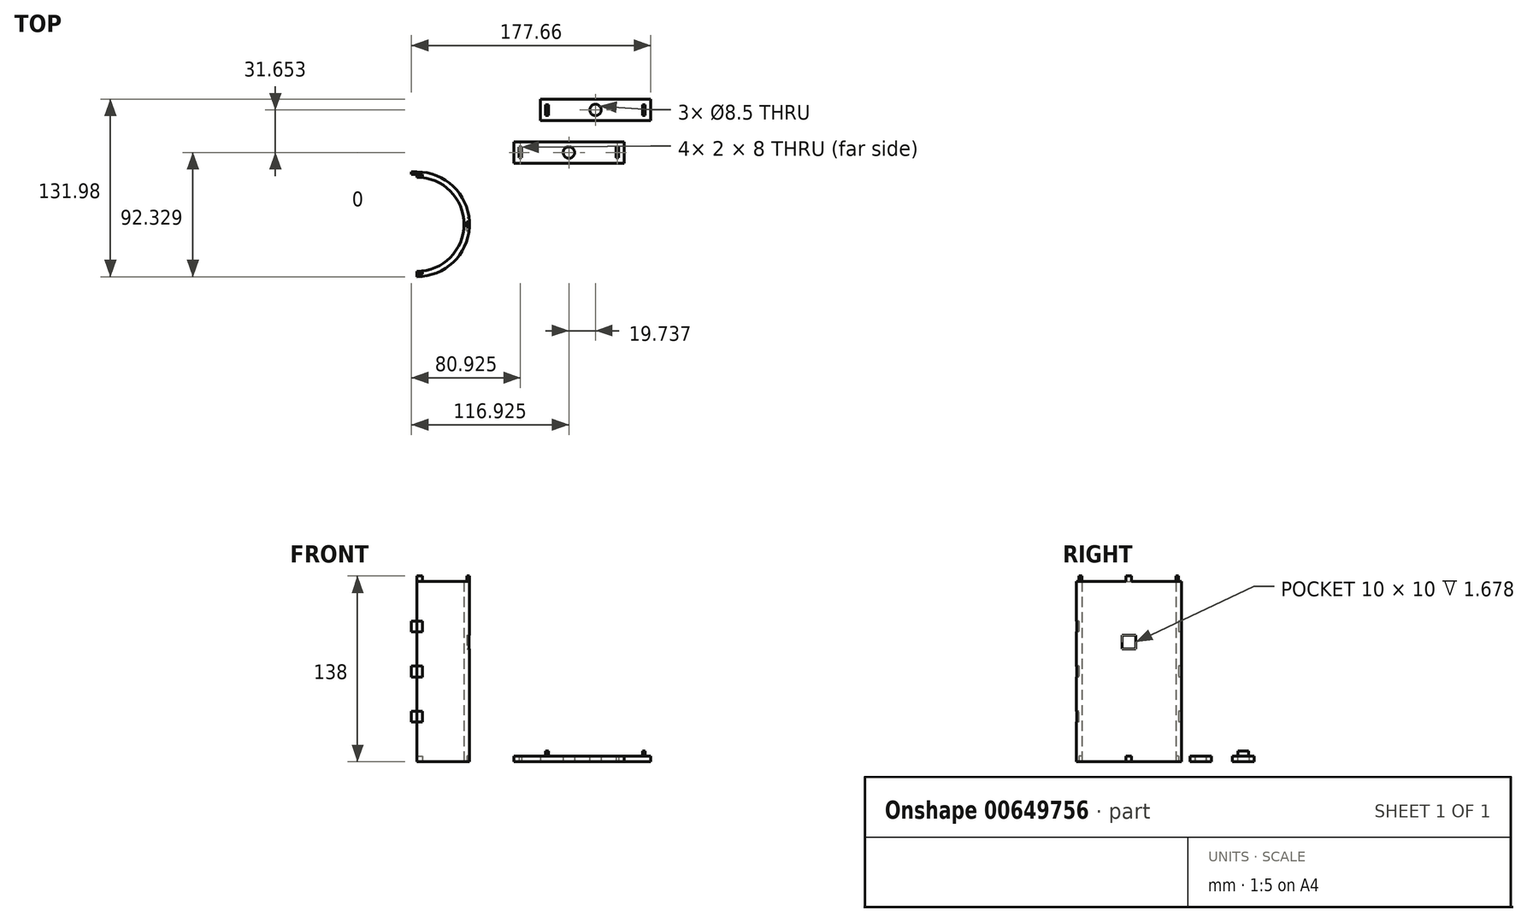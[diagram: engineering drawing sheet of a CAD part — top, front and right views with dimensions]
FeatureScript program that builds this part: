
annotation { "Feature Type Name" : "Feature", "Feature Type Description" : "" }
export const myFeature = defineFeature(function(context is Context, id is Id, definition is map)
    precondition{}
    {
        {
            var Q0;
            Q0=qCreatedBy(makeId("Top.planeOp"),FACE);
            var sketch = newSketch(context, id + "F0", { "sketchPlane" : qUnion([Q0])});
            skCircle(sketch, "E0", {"center": v(0, 0) * mm, "radius": 35 * mm});
            skCircle(sketch, "E1", {"center": v(0, 0) * mm, "radius": 39 * mm});
            skLineSegment(sketch, "E2", {"start": v(0, 39) * mm, "end": v(0, -39) * mm});
            skPoint(sketch, "E3", {"position": v(0, 35) * mm});
            skPoint(sketch, "E4", {"position": v(0, -35) * mm});
            skLineSegment(sketch, "E5.bottom", {"start": v(0, 35) * mm, "end": v(4, 35) * mm});
            skLineSegment(sketch, "E5.top", {"start": v(0, 37) * mm, "end": v(4, 37) * mm});
            skLineSegment(sketch, "E5.left", {"start": v(0, 35) * mm, "end": v(0, 37) * mm});
            skLineSegment(sketch, "E5.right", {"start": v(4, 35) * mm, "end": v(4, 37) * mm});
            skLineSegment(sketch, "E6.bottom", {"start": v(0, -35) * mm, "end": v(4, -35) * mm});
            skLineSegment(sketch, "E6.top", {"start": v(0, -37) * mm, "end": v(4, -37) * mm});
            skLineSegment(sketch, "E6.left", {"start": v(0, -35) * mm, "end": v(0, -37) * mm});
            skLineSegment(sketch, "E6.right", {"start": v(4, -35) * mm, "end": v(4, -37) * mm});
            skLineSegment(sketch, "E7", {"start": v(0, 0) * mm, "end": v(39, 0) * mm, "construction": true});
            skLineSegment(sketch, "E8.bottom", {"start": v(39, 2) * mm, "end": v(37, 2) * mm});
            skLineSegment(sketch, "E8.top", {"start": v(39, -2) * mm, "end": v(37, -2) * mm});
            skLineSegment(sketch, "E8.left", {"start": v(39, 2) * mm, "end": v(39, -2) * mm});
            skLineSegment(sketch, "E8.right", {"start": v(37, 2) * mm, "end": v(37, -2) * mm});
            skPoint(sketch, "E9", {"position": v(39, 0) * mm});
            skSolve(sketch);
        }
        {
            var Q0;
            {var subQ2=sQuery(id+"F0.wireOp",EDGE,"E5.bottom");Q0=makeQuery(id+"F0.imprint","IMPRINT",FACE,{"disambiguationData":[TD([[makeQuery(id+"F0.imprint","IMPRINT",EDGE,{"derivedFrom":subQ2}),-1.0]])]});}
            var Q1;
            Q1=makeQuery(id+"F0.imprint","IMPRINT",FACE,{"disambiguationData":[TD([[makeQuery(id+"F0.imprint","IMPRINT",EDGE,{"derivedFrom":sQuery(id+"F0.wireOp",EDGE,"E6.bottom")}),-1.0]])]});
            var Q2;
            Q2=makeQuery(id+"F0.imprint","IMPRINT",FACE,{"disambiguationData":[TD([[makeQuery(id+"F0.imprint","IMPRINT",EDGE,{"derivedFrom":sQuery(id+"F0.wireOp",EDGE,"E5.bottom")}),1.0]])]});
            var Q3;
            {var subQ0=sQuery(id+"F0.wireOp",EDGE,"E8.right");Q3=makeQuery(id+"F0.imprint","IMPRINT",FACE,{"disambiguationData":[TD([[makeQuery(id+"F0.imprint","IMPRINT",EDGE,{"derivedFrom":subQ0}),1.0]])]});}
            extrude(context, id + "F1", {"entities" : qUnion([Q0, Q1, Q2, Q3]), "depth" : 134 * mm, "offsetDistance" : 25 * mm});
        }
        {
            var Q0;
            Q0=makeQuery(id+"F0.imprint","IMPRINT",FACE,{"disambiguationData":[TD([[makeQuery(id+"F0.imprint","IMPRINT",EDGE,{"derivedFrom":sQuery(id+"F0.wireOp",EDGE,"E6.bottom")}),-1.0]])]});
            var Q1;
            {var subQ0=sQuery(id+"F0.wireOp",EDGE,"E8.right");Q1=makeQuery(id+"F0.imprint","IMPRINT",FACE,{"disambiguationData":[TD([[makeQuery(id+"F0.imprint","IMPRINT",EDGE,{"derivedFrom":subQ0}),1.0]])]});}
            var Q2;
            Q2=makeQuery(id+"F0.imprint","IMPRINT",FACE,{"disambiguationData":[TD([[makeQuery(id+"F0.imprint","IMPRINT",EDGE,{"derivedFrom":sQuery(id+"F0.wireOp",EDGE,"E5.bottom")}),1.0]])]});
            extrude(context, id + "F2", {"entities" : qUnion([Q0, Q1, Q2]), "operationType" : NewBodyOperationType.ADD, "depth" : 138 * mm, "offsetDistance" : 25 * mm});
        }
        {
            var Q0;
            Q0=makeQuery(id+"F0.imprint","IMPRINT",FACE,{"disambiguationData":[TD([[makeQuery(id+"F0.imprint","IMPRINT",EDGE,{"derivedFrom":sQuery(id+"F0.wireOp",EDGE,"E6.bottom")}),-1.0]])]});
            var Q1;
            {var subQ0=sQuery(id+"F0.wireOp",EDGE,"E8.right");Q1=makeQuery(id+"F0.imprint","IMPRINT",FACE,{"disambiguationData":[TD([[makeQuery(id+"F0.imprint","IMPRINT",EDGE,{"derivedFrom":subQ0}),1.0]])]});}
            var Q2;
            Q2=makeQuery(id+"F0.imprint","IMPRINT",FACE,{"disambiguationData":[TD([[makeQuery(id+"F0.imprint","IMPRINT",EDGE,{"derivedFrom":sQuery(id+"F0.wireOp",EDGE,"E5.bottom")}),1.0]])]});
            extrude(context, id + "F3", {"entities" : qUnion([Q0, Q1, Q2]), "operationType" : NewBodyOperationType.REMOVE, "oppositeDirection" : true, "depth" : 4 * mm, "offsetDistance" : 25 * mm});
        }
        {
            var Q0;
            Q0=makeQuery(id+"F0.imprint","IMPRINT",FACE,{"disambiguationData":[TD([[makeQuery(id+"F0.imprint","IMPRINT",EDGE,{"derivedFrom":sQuery(id+"F0.wireOp",EDGE,"E6.bottom")}),-1.0]])]});
            var Q1;
            {var subQ0=sQuery(id+"F0.wireOp",EDGE,"E8.right");Q1=makeQuery(id+"F0.imprint","IMPRINT",FACE,{"disambiguationData":[TD([[makeQuery(id+"F0.imprint","IMPRINT",EDGE,{"derivedFrom":subQ0}),1.0]])]});}
            var Q2;
            Q2=makeQuery(id+"F0.imprint","IMPRINT",FACE,{"disambiguationData":[TD([[makeQuery(id+"F0.imprint","IMPRINT",EDGE,{"derivedFrom":sQuery(id+"F0.wireOp",EDGE,"E5.bottom")}),1.0]])]});
            extrude(context, id + "F4", {"entities" : qUnion([Q0, Q1, Q2]), "operationType" : NewBodyOperationType.REMOVE, "oppositeDirection" : true, "depth" : -4 * mm, "offsetDistance" : 25 * mm});
        }
        {
            var Q0;
            {var subQ0=sQuery(id+"F0.wireOp",EDGE,"E5.left");Q0=makeQuery(id+"F2.boolean.opBoolean","MERGE",FACE,{"derivedFrom":[makeQuery(id+"F1.opExtrude","SWEPT_FACE",FACE,{"disambiguationData":[OSD([sQuery(id+"F0.wireOp",EDGE,"E2"),subQ0])]}),makeQuery(id+"F2.opExtrude","SWEPT_FACE",FACE,{"disambiguationData":[OSD([subQ0])]})]});}
            var sketch = newSketch(context, id + "F5", { "sketchPlane" : qUnion([Q0])});
            skLineSegment(sketch, "E10", {"start": v(-39, 134) * mm, "end": v(-39, 0) * mm, "construction": true});
            skPoint(sketch, "E11", {"position": v(-39, 67) * mm});
            skLineSegment(sketch, "E12", {"start": v(-39, 0) * mm, "end": v(39, 0) * mm, "construction": true});
            skLineSegment(sketch, "E13", {"start": v(39, 134) * mm, "end": v(39, 0) * mm, "construction": true});
            skPoint(sketch, "E14", {"position": v(39, 67) * mm});
            skLineSegment(sketch, "E15.bottom", {"start": v(-39, 71) * mm, "end": v(-37, 71) * mm});
            skLineSegment(sketch, "E15.top", {"start": v(-39, 63) * mm, "end": v(-37, 63) * mm});
            skLineSegment(sketch, "E15.left", {"start": v(-39, 71) * mm, "end": v(-39, 63) * mm});
            skLineSegment(sketch, "E15.right", {"start": v(-37, 71) * mm, "end": v(-37, 63) * mm});
            skLineSegment(sketch, "E16.bottom", {"start": v(37, 71) * mm, "end": v(39, 71) * mm});
            skLineSegment(sketch, "E16.top", {"start": v(37, 63) * mm, "end": v(39, 63) * mm});
            skLineSegment(sketch, "E16.left", {"start": v(37, 71) * mm, "end": v(37, 63) * mm});
            skLineSegment(sketch, "E16.right", {"start": v(39, 71) * mm, "end": v(39, 63) * mm});
            skPoint(sketch, "E17", {"position": v(-39, 100.5) * mm});
            skPoint(sketch, "E18", {"position": v(39, 100.5) * mm});
            skPoint(sketch, "E19", {"position": v(39, 33.5) * mm});
            skPoint(sketch, "E20", {"position": v(-39, 33.5) * mm});
            skLineSegment(sketch, "E21.bottom", {"start": v(-39, 104.5) * mm, "end": v(-37, 104.5) * mm});
            skLineSegment(sketch, "E21.top", {"start": v(-39, 96.5) * mm, "end": v(-37, 96.5) * mm});
            skLineSegment(sketch, "E21.left", {"start": v(-39, 104.5) * mm, "end": v(-39, 96.5) * mm});
            skLineSegment(sketch, "E21.right", {"start": v(-37, 104.5) * mm, "end": v(-37, 96.5) * mm});
            skLineSegment(sketch, "E22.bottom", {"start": v(-39, 37.5) * mm, "end": v(-37, 37.5) * mm});
            skLineSegment(sketch, "E22.top", {"start": v(-39, 29.5) * mm, "end": v(-37, 29.5) * mm});
            skLineSegment(sketch, "E22.left", {"start": v(-39, 37.5) * mm, "end": v(-39, 29.5) * mm});
            skLineSegment(sketch, "E22.right", {"start": v(-37, 37.5) * mm, "end": v(-37, 29.5) * mm});
            skLineSegment(sketch, "E23.bottom", {"start": v(37, 104.5) * mm, "end": v(39, 104.5) * mm});
            skLineSegment(sketch, "E23.top", {"start": v(37, 96.5) * mm, "end": v(39, 96.5) * mm});
            skLineSegment(sketch, "E23.left", {"start": v(37, 104.5) * mm, "end": v(37, 96.5) * mm});
            skLineSegment(sketch, "E23.right", {"start": v(39, 104.5) * mm, "end": v(39, 96.5) * mm});
            skLineSegment(sketch, "E24.bottom", {"start": v(37, 29.5) * mm, "end": v(39, 29.5) * mm});
            skLineSegment(sketch, "E24.top", {"start": v(37, 37.5) * mm, "end": v(39, 37.5) * mm});
            skLineSegment(sketch, "E24.left", {"start": v(37, 29.5) * mm, "end": v(37, 37.5) * mm});
            skLineSegment(sketch, "E24.right", {"start": v(39, 29.5) * mm, "end": v(39, 37.5) * mm});
            skSolve(sketch);
        }
        {
            var Q0;
            Q0=makeQuery(id+"F5.imprint","IMPRINT",FACE,{"disambiguationData":[TD([[makeQuery(id+"F5.imprint","IMPRINT",EDGE,{"derivedFrom":sQuery(id+"F5.wireOp",EDGE,"E21.bottom")}),-1.0]])]});
            var Q1;
            Q1=makeQuery(id+"F5.imprint","IMPRINT",FACE,{"disambiguationData":[TD([[makeQuery(id+"F5.imprint","IMPRINT",EDGE,{"derivedFrom":sQuery(id+"F5.wireOp",EDGE,"E15.bottom")}),-1.0]])]});
            var Q2;
            Q2=makeQuery(id+"F5.imprint","IMPRINT",FACE,{"disambiguationData":[TD([[makeQuery(id+"F5.imprint","IMPRINT",EDGE,{"derivedFrom":sQuery(id+"F5.wireOp",EDGE,"E22.bottom")}),-1.0]])]});
            extrude(context, id + "F6", {"entities" : qUnion([Q0, Q1, Q2]), "operationType" : NewBodyOperationType.ADD, "depth" : 4 * mm, "offsetDistance" : 25 * mm});
        }
        {
            var Q0;
            Q0=makeQuery(id+"F5.imprint","IMPRINT",FACE,{"disambiguationData":[TD([[makeQuery(id+"F5.imprint","IMPRINT",EDGE,{"derivedFrom":sQuery(id+"F5.wireOp",EDGE,"E23.bottom")}),-1.0]])]});
            var Q1;
            Q1=makeQuery(id+"F5.imprint","IMPRINT",FACE,{"disambiguationData":[TD([[makeQuery(id+"F5.imprint","IMPRINT",EDGE,{"derivedFrom":sQuery(id+"F5.wireOp",EDGE,"E16.bottom")}),-1.0]])]});
            var Q2;
            Q2=makeQuery(id+"F5.imprint","IMPRINT",FACE,{"disambiguationData":[TD([[makeQuery(id+"F5.imprint","IMPRINT",EDGE,{"derivedFrom":sQuery(id+"F5.wireOp",EDGE,"E24.bottom")}),1.0]])]});
            extrude(context, id + "F7", {"entities" : qUnion([Q0, Q1, Q2]), "operationType" : NewBodyOperationType.REMOVE, "oppositeDirection" : true, "depth" : 4 * mm, "offsetDistance" : 25 * mm});
        }
        {
            var Q0;
            Q0=qCreatedBy(makeId("Right.planeOp"),FACE);
            cPlane(context, id + "F8", {"entities" : qUnion([Q0]), "cplaneType" : CPlaneType.OFFSET, "offset" : 39 * mm, "width" : 150 * mm, "height" : 150 * mm});
        }
        {
            var Q0;
            Q0=qCreatedBy(id+"F8.planeOp",FACE);
            var sketch = newSketch(context, id + "F9", { "sketchPlane" : qUnion([Q0])});
            skLineSegment(sketch, "E25.bottom", {"start": v(-5, 94) * mm, "end": v(5, 94) * mm});
            skLineSegment(sketch, "E25.top", {"start": v(-5, 84) * mm, "end": v(5, 84) * mm});
            skLineSegment(sketch, "E25.left", {"start": v(-5, 94) * mm, "end": v(-5, 84) * mm});
            skLineSegment(sketch, "E25.right", {"start": v(5, 94) * mm, "end": v(5, 84) * mm});
            skLineSegment(sketch, "E26", {"start": v(0, 0) * mm, "end": v(0, 134) * mm, "construction": true});
            skPoint(sketch, "E27", {"position": v(0, 94) * mm});
            skSolve(sketch);
        }
        {
            var Q0;
            Q0=makeQuery(id+"F9.imprint","IMPRINT",FACE,{"disambiguationData":[TD([[makeQuery(id+"F9.imprint","IMPRINT",EDGE,{"derivedFrom":sQuery(id+"F9.wireOp",EDGE,"E25.bottom")}),-1.0]])]});
            extrude(context, id + "F10", {"entities" : qUnion([Q0]), "operationType" : NewBodyOperationType.REMOVE, "oppositeDirection" : true, "depth" : 2 * mm, "offsetDistance" : 25 * mm});
        }
        {
            var Q0;
            Q0=qCreatedBy(makeId("Top.planeOp"),FACE);
            var sketch = newSketch(context, id + "F11", { "sketchPlane" : qUnion([Q0])});
            skLineSegment(sketch, "E28.bottom", {"start": v(153.92, 45.33) * mm, "end": v(71.92, 45.33) * mm});
            skLineSegment(sketch, "E28.top", {"start": v(153.92, 61.33) * mm, "end": v(71.92, 61.33) * mm});
            skLineSegment(sketch, "E28.left", {"start": v(153.92, 45.33) * mm, "end": v(153.92, 61.33) * mm});
            skLineSegment(sketch, "E28.right", {"start": v(71.92, 45.33) * mm, "end": v(71.92, 61.33) * mm});
            skLineSegment(sketch, "E29.bottom", {"start": v(149.92, 49.33) * mm, "end": v(147.92, 49.33) * mm});
            skLineSegment(sketch, "E29.top", {"start": v(149.92, 57.33) * mm, "end": v(147.92, 57.33) * mm});
            skLineSegment(sketch, "E29.left", {"start": v(149.92, 49.33) * mm, "end": v(149.92, 57.33) * mm});
            skLineSegment(sketch, "E29.right", {"start": v(147.92, 49.33) * mm, "end": v(147.92, 57.33) * mm});
            skLineSegment(sketch, "E30.bottom", {"start": v(77.92, 49.33) * mm, "end": v(75.92, 49.33) * mm});
            skLineSegment(sketch, "E30.top", {"start": v(77.92, 57.33) * mm, "end": v(75.92, 57.33) * mm});
            skLineSegment(sketch, "E30.left", {"start": v(77.92, 49.33) * mm, "end": v(77.92, 57.33) * mm});
            skLineSegment(sketch, "E30.right", {"start": v(75.92, 49.33) * mm, "end": v(75.92, 57.33) * mm});
            skPoint(sketch, "E31", {"position": v(112.92, 45.33) * mm});
            skPoint(sketch, "E32", {"position": v(153.92, 53.33) * mm});
            skLineSegment(sketch, "E33", {"start": v(153.92, 53.33) * mm, "end": v(112.92, 53.33) * mm, "construction": true});
            skLineSegment(sketch, "E34", {"start": v(112.92, 45.33) * mm, "end": v(112.92, 53.33) * mm, "construction": true});
            skCircle(sketch, "E35", {"center": v(112.92, 53.33) * mm, "radius": 4.25 * mm});
            skLineSegment(sketch, "E36.bottom", {"start": v(173.66, 76.98) * mm, "end": v(91.66, 76.98) * mm});
            skLineSegment(sketch, "E36.top", {"start": v(173.66, 92.98) * mm, "end": v(91.66, 92.98) * mm});
            skLineSegment(sketch, "E36.left", {"start": v(173.66, 76.98) * mm, "end": v(173.66, 92.98) * mm});
            skLineSegment(sketch, "E36.right", {"start": v(91.66, 76.98) * mm, "end": v(91.66, 92.98) * mm});
            skLineSegment(sketch, "E37.bottom", {"start": v(169.66, 80.98) * mm, "end": v(167.66, 80.98) * mm});
            skLineSegment(sketch, "E37.top", {"start": v(169.66, 88.98) * mm, "end": v(167.66, 88.98) * mm});
            skLineSegment(sketch, "E37.left", {"start": v(169.66, 80.98) * mm, "end": v(169.66, 88.98) * mm});
            skLineSegment(sketch, "E37.right", {"start": v(167.66, 80.98) * mm, "end": v(167.66, 88.98) * mm});
            skLineSegment(sketch, "E38.bottom", {"start": v(97.66, 80.98) * mm, "end": v(95.66, 80.98) * mm});
            skLineSegment(sketch, "E38.top", {"start": v(97.66, 88.98) * mm, "end": v(95.66, 88.98) * mm});
            skLineSegment(sketch, "E38.left", {"start": v(97.66, 80.98) * mm, "end": v(97.66, 88.98) * mm});
            skLineSegment(sketch, "E38.right", {"start": v(95.66, 80.98) * mm, "end": v(95.66, 88.98) * mm});
            skPoint(sketch, "E39", {"position": v(132.66, 76.98) * mm});
            skPoint(sketch, "E40", {"position": v(173.66, 84.98) * mm});
            skLineSegment(sketch, "E41", {"start": v(173.66, 84.98) * mm, "end": v(132.66, 84.98) * mm, "construction": true});
            skLineSegment(sketch, "E42", {"start": v(132.66, 76.98) * mm, "end": v(132.66, 84.98) * mm, "construction": true});
            skCircle(sketch, "E43", {"center": v(132.66, 84.98) * mm, "radius": 4.25 * mm});
            skSolve(sketch);
        }
        {
            var Q0;
            Q0=makeQuery(id+"F11.imprint","IMPRINT",FACE,{"disambiguationData":[TD([[makeQuery(id+"F11.imprint","IMPRINT",EDGE,{"derivedFrom":sQuery(id+"F11.wireOp",EDGE,"E28.bottom")}),-1.0]])]});
            extrude(context, id + "F12", {"entities" : qUnion([Q0]), "depth" : 4 * mm, "offsetDistance" : 25 * mm});
        }
        {
            var Q0;
            Q0=makeQuery(id+"F11.imprint","IMPRINT",FACE,{"disambiguationData":[TD([[makeQuery(id+"F11.imprint","IMPRINT",EDGE,{"derivedFrom":sQuery(id+"F11.wireOp",EDGE,"E36.bottom")}),-1.0]])]});
            extrude(context, id + "F13", {"entities" : qUnion([Q0]), "depth" : 4 * mm, "offsetDistance" : 25 * mm});
        }
        {
            var Q0;
            Q0=makeQuery(id+"F11.imprint","IMPRINT",FACE,{"disambiguationData":[TD([[makeQuery(id+"F11.imprint","IMPRINT",EDGE,{"derivedFrom":sQuery(id+"F11.wireOp",EDGE,"E37.bottom")}),-1.0]])]});
            var Q1;
            Q1=makeQuery(id+"F11.imprint","IMPRINT",FACE,{"disambiguationData":[TD([[makeQuery(id+"F11.imprint","IMPRINT",EDGE,{"derivedFrom":sQuery(id+"F11.wireOp",EDGE,"E38.bottom")}),-1.0]])]});
            extrude(context, id + "F14", {"entities" : qUnion([Q0, Q1]), "operationType" : NewBodyOperationType.ADD, "depth" : 8 * mm, "offsetDistance" : 25 * mm});
        }
    });
